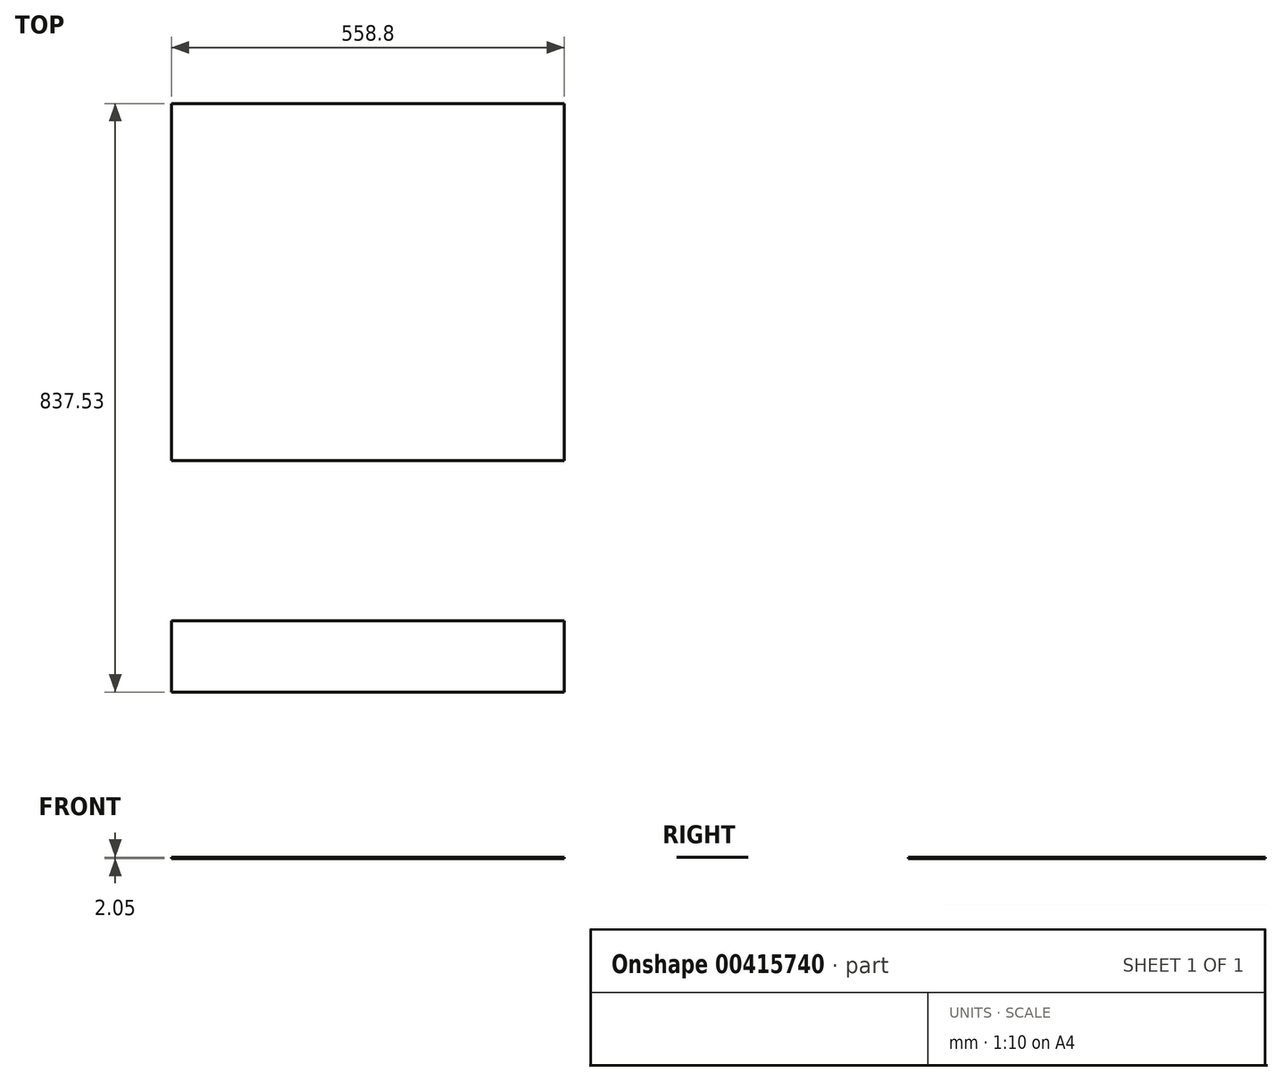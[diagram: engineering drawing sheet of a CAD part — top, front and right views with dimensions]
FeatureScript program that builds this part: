
annotation { "Feature Type Name" : "Feature", "Feature Type Description" : "" }
export const myFeature = defineFeature(function(context is Context, id is Id, definition is map)
    precondition{}
    {
        {
            var Q0;
            Q0=qCreatedBy(makeId("Top.planeOp"),FACE);
            var sketch = newSketch(context, id + "F0", { "sketchPlane" : qUnion([Q0])});
            skLineSegment(sketch, "E0.bottom", {"start": v(279.4, -254) * mm, "end": v(-279.4, -254) * mm});
            skLineSegment(sketch, "E0.top", {"start": v(279.4, 254) * mm, "end": v(-279.4, 254) * mm});
            skLineSegment(sketch, "E0.left", {"start": v(279.4, -254) * mm, "end": v(279.4, 254) * mm});
            skLineSegment(sketch, "E0.right", {"start": v(-279.4, -254) * mm, "end": v(-279.4, 254) * mm});
            skPoint(sketch, "E0.middle", {"position": v(0, 0) * mm});
            skSolve(sketch);
        }
        {
            var Q0;
            Q0=makeQuery(id+"F0.imprint","IMPRINT",FACE,{"disambiguationData":[TD([[makeQuery(id+"F0.imprint","IMPRINT",EDGE,{"derivedFrom":sQuery(id+"F0.wireOp",EDGE,"E0.bottom")}),-1.0]])]});
            extrude(context, id + "F1", {"entities" : qUnion([Q0]), "depth" : 2.03 * mm});
        }
        {
            var Q0;
            Q0=makeQuery(id+"F1.opExtrude","CAP_FACE",FACE,{"disambiguationData":[OSD([sQuery(id+"F0.wireOp",EDGE,"E0.bottom"),sQuery(id+"F0.wireOp",EDGE,"E0.top"),sQuery(id+"F0.wireOp",EDGE,"E0.left"),sQuery(id+"F0.wireOp",EDGE,"E0.right")])],"isStart":false});
            var sketch = newSketch(context, id + "F2", { "sketchPlane" : qUnion([Q0])});
            skLineSegment(sketch, "E1.bottom", {"start": v(279.4, -583.53) * mm, "end": v(-279.4, -583.53) * mm});
            skLineSegment(sketch, "E1.top", {"start": v(279.4, -481.93) * mm, "end": v(-279.4, -481.93) * mm});
            skLineSegment(sketch, "E1.left", {"start": v(279.4, -583.53) * mm, "end": v(279.4, -481.93) * mm});
            skLineSegment(sketch, "E1.right", {"start": v(-279.4, -583.53) * mm, "end": v(-279.4, -481.93) * mm});
            skPoint(sketch, "E1.middle", {"position": v(0, -532.73) * mm});
            skPoint(sketch, "E1.middle.positionSnap0", {"position": v(0, -254) * mm});
            skPoint(sketch, "E1.centerSnap0", {"position": v(0, -254) * mm});
            skSolve(sketch);
        }
        {
            var Q0;
            Q0=makeQuery(id+"F2.imprint","IMPRINT",FACE,{"disambiguationData":[TD([[makeQuery(id+"F2.imprint","IMPRINT",EDGE,{"derivedFrom":sQuery(id+"F2.wireOp",EDGE,"E1.bottom")}),-1.0]])]});
            extrude(context, id + "F3", {"entities" : qUnion([Q0]), "depth" : 1 / 50.8 * mm});
        }
        {
            var Q0;
            Q0=makeQuery(id+"F3.opExtrude","CAP_EDGE",EDGE,{"disambiguationData":[OSD([sQuery(id+"F2.wireOp",EDGE,"E1.bottom")])],"isStart":true});
            fillet(context, id + "F4", {"entities" : qUnion([Q0]), "radius" : 5.08 * mm, "tangentPropagation" : true, "allowEdgeOverflow" : false});
        }
    });
